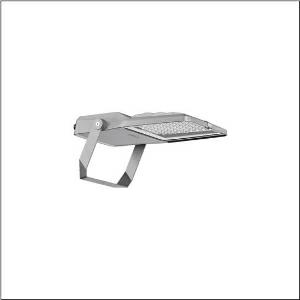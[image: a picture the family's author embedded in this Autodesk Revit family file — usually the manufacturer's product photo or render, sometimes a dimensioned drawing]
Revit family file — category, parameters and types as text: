
# Revit family: floodlight_fl_21_iq_mini___pl33t_5xa7772d3f1a_bc4e
name_source: partatom
category: Lighting Fixtures
units: mm (PartAtom-declared; Revit-internal decimal feet)

## family parameters
Cut with Voids When Loaded = No
Host = Face
Light Source = No
Part Type = Normal
Room Calculation Point = No
Round Connector Dimension = Use Diameter
Shared = No

## types (1)
- --- (1 x LED, 15160 lm, 143 W, 3000K)
    Apparent Load = 143 VA
    CIE Flux Codes = 26 75 99 100 100
    Color Rendering = 80
    Color Temperature = 3000K
    Default Elevation = 1800 mm
    Description = Floodlight FL 21 iQ mini, floodlight, primary light control with lens, of PMMA, primary optical cover: protective disc, of toughened safety glass, transparent, light distribution: PL33T, light emission: direct distribution, installation type: surface-mounted, lamps: LED, High Power LED, rated values: 15.160lm | 143W | 106lm/W (begin service life); end service life: 15.160lm | 151,6W; at 50% lumin. flux: 7.580lm | 60,5W | 125,3lm/W, colour temperature: 3000K, colour rendering: CRI > 80, light colour: 830, light setting 1 begin service life: 100% | 15.160lm | 143W | 106lm/W | 3.000K, light setting 1 end service life: 151,6W, further light settings possible, control: Street-Remote, Auto-Match, Temp-Guard, Night-Set, Smart-Wire, Desk-Remote (wireless, voltage-free reading and setting of iQ features in the workshop via application-optimized NFC function/RFID function), optimised constant luminous flux control (CLO 2.0), pre-setting: linear dimming characteristic, with terminal, 6-pole, mains connection: 220..240V, AC, 50/60Hz, luminaire housing, of diecast aluminium, powder-coated, SITECO metallic grey (DB 702S), corrosivity category C5 mid according to DIN EN ISO 12944suitable for swimming poolschlorine-resistant, sealing non-destructively replaceable, mounting bracket, of steel, galvanised, powder-coated, SITECO metallic grey (DB 702S), protection rating (complete): IP66, insulation class (complete): insulation class II (safety insulation), certification: CE, ENEC, VDE, protection symbol: D, impact resistance: IK08, permissible operating ambient temperature: -40..+40°C, permissible operating ambient temperature for outdoor applications: -40..+50°C, standard: DIN EN 12944, LABS conformity tested according to VDMA 24364:2018-05, packaging unit: 1 piece

Light Distribution: PL33T
    Height = 70 mm
    Lamp = 1 x LED
    Lamp Light Flux = 15160 lm
    Lamp Power = 143 W
    Lamp count = 1
    Length = 485 mm
    Luminous efficacy = 106 lm/W
    Manufacturer = Siteco
    ModVariant = No
    Model = 5XA7772D3F1A
    Number of Poles = 1
    OnlyDefault = Yes
    Power Factor = 1
    Product Name = Floodlight FL 21 iQ mini | PL33T
    Product group = floodlight | pylon annexe
    ProductGroupID = 6201
    Protection Class = Protection class II
    Protection Degree = IP 66
    RLX_Detail_Level = 1
    RLX_Emergency_Light_Flux = 0 lm
    RLX_Emergency_Type = 0
    RLX_Emergency_Type_DB = No
    RlxData = <blob elided: 96617 chars, md5=1bf757b7>
    Socket = socket
    Standby Power = 0 W
    System Light Flux = 15160 lm
    System Power = 143 W
    Type Comments = factory setting: luminous flux: 100 % | dim-lin: 254 | 730 mA
    Type Image = l_1006845.jpg
    URL = http://relux.com
    VarID = @adj_148389
    Voltage = 0 V
    Weight = 0.00 kg
    Width = 337 mm

## geometry (parser evidence)
native form markers: Blend x4, Sweep x12
no freeform markers — native parametric forms only
